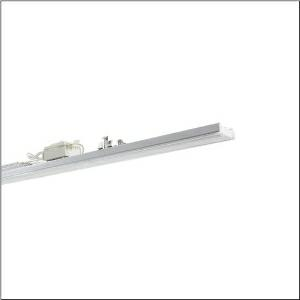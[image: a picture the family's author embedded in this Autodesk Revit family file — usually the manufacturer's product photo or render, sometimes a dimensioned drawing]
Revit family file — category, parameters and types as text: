
# Revit family: licross_21_recessed_mo_52te18cn49xg
name_source: partatom
category: Lighting Fixtures
units: mm (PartAtom-declared; Revit-internal decimal feet)

## family parameters
Cut with Voids When Loaded = No
Host = Face
Light Source = No
Part Type = Normal
Room Calculation Point = No
Round Connector Dimension = Use Diameter
Shared = No

## types (1)
- --- (1 x LED, 9000 lm, 49.9 W, 4000K)
    Apparent Load = 50 VA
    CIE Flux Codes = 79 95 99 100 100
    Color Rendering = 80
    Color Temperature = 4000K
    Default Elevation = 1800 mm
    Description = Licross 21 Recessed MO, luminaire insert, of sheet steel, galvanised, coil coated, white, length: 1.500mm, width: 66mm, height: 67mm, LED rated luminous flux: 9.000lm, light colour: 840, SDCM (Standard Deviation of Colour Matching)MacAdam ≤ 3 SDCM (initial), control gear: ON/OFF Multilumen, CLOi, with plug, 3-pole, with phase selection, mains connection: 220..240V, AC, 50/60Hz, start of lifetime: 50W, end of service life: 61W, internal wiring halogen-free, primary light control with lens, of plastic, primary optical cover: cover, of PMMA, light emission: direct distribution, primary light characteristic: symmetric, protection rating (complete): IP54, insulation class (complete): insulation class I (protective earthing), certification: CE, ENEC, VDE, UKCA, protection symbol: D if used in an environment with non-conductive dust loads with corresponding accessories, impact resistance: IK06, permissible ambient temperature for indoor applications: -35..+40°C, corresponds to IFS (International Featured Standards) requirements for safety and quality in the food industry, reducing of maximum allowable ambient temperature of 5°C with ceiling mounting, LABS conformity tested according to VDMA 24364:2018-05, The light source and the operating device comply with the requirements of the Ecodesign Regulation (EU) 2019/2020 and are replaceable in accordance with this regulation, packaging unit: 1 piece
    Height = 58 mm
    Lamp = 1 x LED
    Lamp Light Flux = 9000 lm
    Lamp Power = 49.9 W
    Lamp count = 1
    Length = 1500 mm
    Luminous efficacy = 180 lm/W
    Manufacturer = Siteco
    ModVariant = No
    Model = 52TE18CN49XG
    Mounting Place = Ceiling
    Mounting Type = Pendant
    Number of Poles = 1
    OnlyDefault = Yes
    Power Factor = 1
    Product Name = Licross 21 Recessed MO
    Product group = luminaire insert | ceiling pendant
    ProductGroupID = 901
    Protection Class = Protection class I
    Protection Degree = IP 54
    RLX_Detail_Level = 1
    RLX_Emergency_Light_Flux = 0 lm
    RLX_Emergency_Type = 0
    RLX_Emergency_Type_DB = No
    RlxData = <blob elided: 22617 chars, md5=8aaaf854>
    Socket = socket
    Standby Power = 0 W
    System Light Flux = 9000 lm
    System Power = 50 W
    Type Comments = factory setting: luminous flux: 100 % | (A | C | E) | 116 mA
    Type Image = l_1296930.jpg
    URL = http://relux.com
    VarID = @adj_109965
    Voltage = 0 V
    Weight = 0.00 kg
    Width = 66 mm

## geometry (parser evidence)
native form markers: Blend x4, Sweep x9
no freeform markers — native parametric forms only
